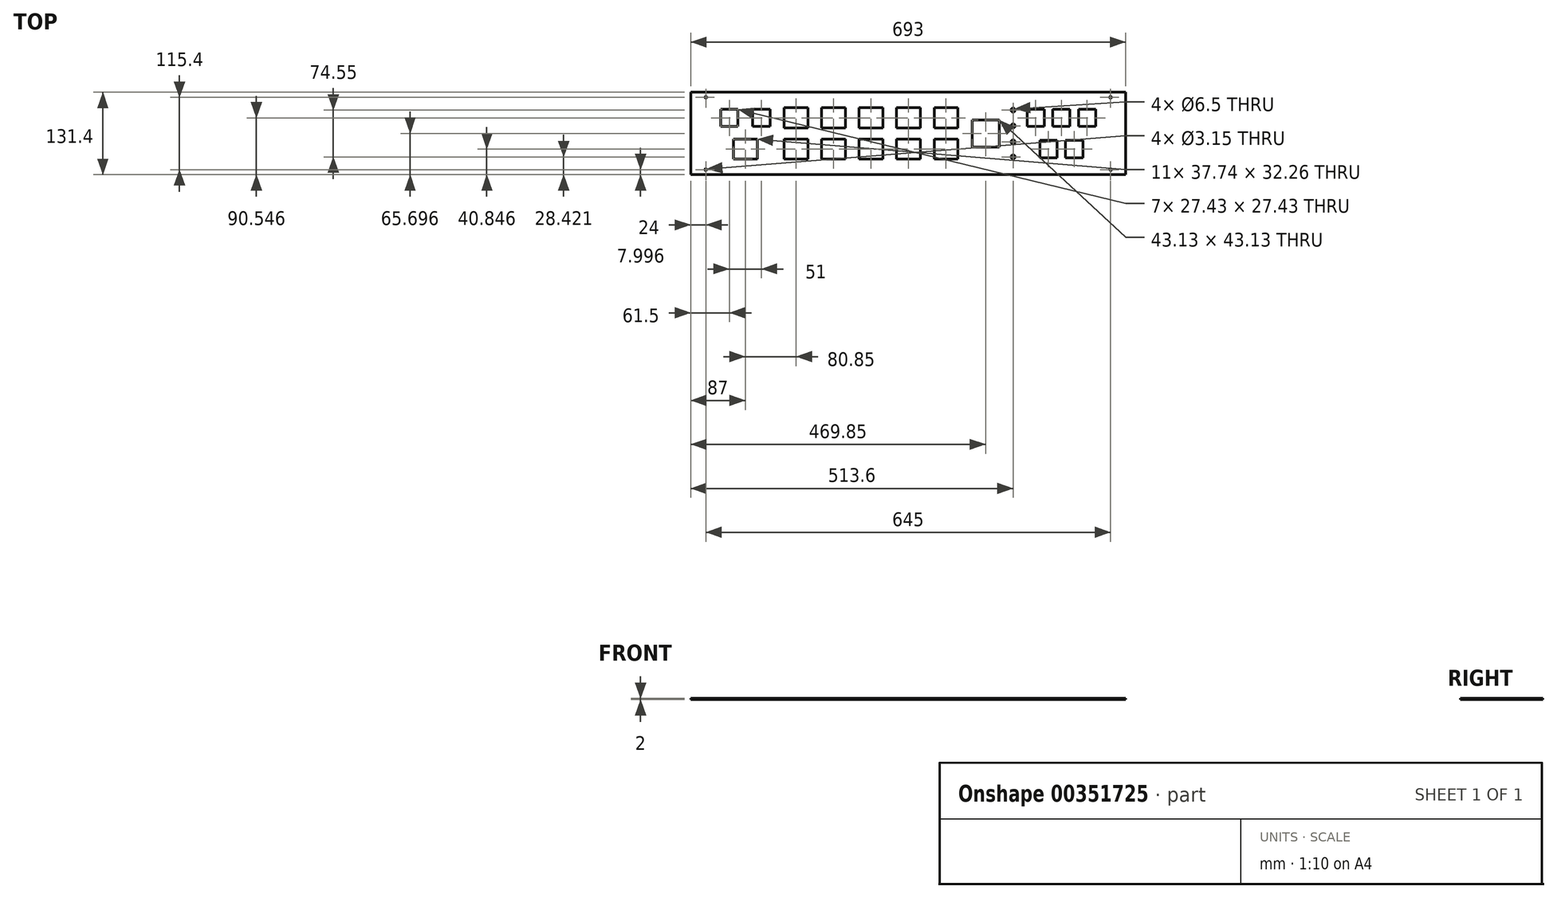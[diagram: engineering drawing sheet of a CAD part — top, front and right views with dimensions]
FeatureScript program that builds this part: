
annotation { "Feature Type Name" : "Feature", "Feature Type Description" : "" }
export const myFeature = defineFeature(function(context is Context, id is Id, definition is map)
    precondition{}
    {
        {
            var Q0;
            Q0=qCreatedBy(makeId("Top.planeOp"),FACE);
            var sketch = newSketch(context, id + "F0", { "sketchPlane" : qUnion([Q0])});
            skLineSegment(sketch, "E0.bottom", {"start": v(-326.44, 13.5) * mm, "end": v(366.56, 13.5) * mm});
            skLineSegment(sketch, "E0.top", {"start": v(-326.44, -117.9) * mm, "end": v(366.56, -117.9) * mm});
            skLineSegment(sketch, "E0.left", {"start": v(-326.44, 13.5) * mm, "end": v(-326.44, -117.9) * mm});
            skLineSegment(sketch, "E0.right", {"start": v(366.56, 13.5) * mm, "end": v(366.56, -117.9) * mm});
            skLineSegment(sketch, "E1", {"start": v(-310.44, 13.5) * mm, "end": v(-310.44, -117.9) * mm, "construction": true});
            skLineSegment(sketch, "E2", {"start": v(350.56, 13.5) * mm, "end": v(350.56, -117.9) * mm, "construction": true});
            skLineSegment(sketch, "E3", {"start": v(-326.44, -2.5) * mm, "end": v(366.56, -2.5) * mm, "construction": true});
            skLineSegment(sketch, "E4", {"start": v(-326.44, -101.9) * mm, "end": v(366.56, -101.9) * mm, "construction": true});
            skLineSegment(sketch, "E5", {"start": v(-326.44, -52.2) * mm, "end": v(366.56, -52.2) * mm, "construction": true});
            skLineSegment(sketch, "E6", {"start": v(-326.44, -27.34) * mm, "end": v(366.56, -27.34) * mm, "construction": true});
            skLineSegment(sketch, "E7", {"start": v(-326.44, -77.04) * mm, "end": v(366.56, -77.04) * mm, "construction": true});
            skLineSegment(sketch, "E8.bottom", {"start": v(-278.65, -13.63) * mm, "end": v(-251.22, -13.63) * mm});
            skLineSegment(sketch, "E8.top", {"start": v(-278.65, -41.06) * mm, "end": v(-251.22, -41.06) * mm});
            skLineSegment(sketch, "E8.left", {"start": v(-278.65, -13.63) * mm, "end": v(-278.65, -41.06) * mm});
            skLineSegment(sketch, "E8.right", {"start": v(-251.22, -13.63) * mm, "end": v(-251.22, -41.06) * mm});
            skLineSegment(sketch, "E9.bottom", {"start": v(-280.44, -11.84) * mm, "end": v(-249.44, -11.84) * mm, "construction": true});
            skLineSegment(sketch, "E9.top", {"start": v(-280.44, -42.84) * mm, "end": v(-249.44, -42.84) * mm, "construction": true});
            skLineSegment(sketch, "E9.left", {"start": v(-280.44, -11.84) * mm, "end": v(-280.44, -42.84) * mm, "construction": true});
            skLineSegment(sketch, "E9.right", {"start": v(-249.44, -11.84) * mm, "end": v(-249.44, -42.84) * mm, "construction": true});
            skLineSegment(sketch, "E10", {"start": v(-251.22, -13.63) * mm, "end": v(-278.65, -41.06) * mm, "construction": true});
            skPoint(sketch, "E11", {"position": v(-264.94, -27.34) * mm});
            skLineSegment(sketch, "E12", {"start": v(-280.44, -11.84) * mm, "end": v(-249.44, -42.84) * mm, "construction": true});
            skLineSegment(sketch, "E13.bottom", {"start": v(-227.65, -13.63) * mm, "end": v(-200.22, -13.63) * mm});
            skLineSegment(sketch, "E13.top", {"start": v(-227.65, -41.06) * mm, "end": v(-200.22, -41.06) * mm});
            skLineSegment(sketch, "E13.left", {"start": v(-227.65, -13.63) * mm, "end": v(-227.65, -41.06) * mm});
            skLineSegment(sketch, "E13.right", {"start": v(-200.22, -13.63) * mm, "end": v(-200.22, -41.06) * mm});
            skLineSegment(sketch, "E14.bottom", {"start": v(-229.44, -11.84) * mm, "end": v(-198.44, -11.84) * mm, "construction": true});
            skLineSegment(sketch, "E14.top", {"start": v(-229.44, -42.84) * mm, "end": v(-198.44, -42.84) * mm, "construction": true});
            skLineSegment(sketch, "E14.left", {"start": v(-229.44, -11.84) * mm, "end": v(-229.44, -42.84) * mm, "construction": true});
            skLineSegment(sketch, "E14.right", {"start": v(-198.44, -11.84) * mm, "end": v(-198.44, -42.84) * mm, "construction": true});
            skLineSegment(sketch, "E15", {"start": v(-200.22, -13.63) * mm, "end": v(-227.65, -41.06) * mm, "construction": true});
            skPoint(sketch, "E16", {"position": v(-213.94, -27.34) * mm});
            skLineSegment(sketch, "E17", {"start": v(-229.44, -11.84) * mm, "end": v(-198.44, -42.84) * mm, "construction": true});
            skLineSegment(sketch, "E18.bottom", {"start": v(-259.29, -59.7) * mm, "end": v(-219.59, -59.7) * mm, "construction": true});
            skLineSegment(sketch, "E18.top", {"start": v(-259.29, -94.4) * mm, "end": v(-219.59, -94.4) * mm, "construction": true});
            skLineSegment(sketch, "E18.left", {"start": v(-259.29, -59.7) * mm, "end": v(-259.29, -94.4) * mm, "construction": true});
            skLineSegment(sketch, "E18.right", {"start": v(-219.59, -59.7) * mm, "end": v(-219.59, -94.4) * mm, "construction": true});
            skLineSegment(sketch, "E19.bottom", {"start": v(-258.3, -60.91) * mm, "end": v(-220.57, -60.91) * mm});
            skLineSegment(sketch, "E19.top", {"start": v(-258.3, -93.17) * mm, "end": v(-220.57, -93.17) * mm});
            skLineSegment(sketch, "E19.left", {"start": v(-258.3, -60.91) * mm, "end": v(-258.3, -93.17) * mm});
            skLineSegment(sketch, "E19.right", {"start": v(-220.57, -60.91) * mm, "end": v(-220.57, -93.17) * mm});
            skLineSegment(sketch, "E20", {"start": v(-259.29, -59.7) * mm, "end": v(-219.59, -94.4) * mm, "construction": true});
            skLineSegment(sketch, "E21", {"start": v(-220.57, -60.91) * mm, "end": v(-258.3, -93.17) * mm, "construction": true});
            skPoint(sketch, "E22", {"position": v(-239.44, -77.04) * mm});
            skLineSegment(sketch, "E23", {"start": v(-249.44, -11.84) * mm, "end": v(-229.44, -11.84) * mm, "construction": true});
            skPoint(sketch, "E24", {"position": v(-239.44, -11.84) * mm});
            skLineSegment(sketch, "E25", {"start": v(-239.44, -11.84) * mm, "end": v(-239.44, -77.04) * mm, "construction": true});
            skLineSegment(sketch, "E26.bottom", {"start": v(-178.44, -59.7) * mm, "end": v(-138.74, -59.7) * mm, "construction": true});
            skLineSegment(sketch, "E26.top", {"start": v(-178.44, -94.4) * mm, "end": v(-138.74, -94.4) * mm, "construction": true});
            skLineSegment(sketch, "E26.left", {"start": v(-178.44, -59.7) * mm, "end": v(-178.44, -94.4) * mm, "construction": true});
            skLineSegment(sketch, "E26.right", {"start": v(-138.74, -59.7) * mm, "end": v(-138.74, -94.4) * mm, "construction": true});
            skLineSegment(sketch, "E27.bottom", {"start": v(-177.46, -60.91) * mm, "end": v(-139.72, -60.91) * mm});
            skLineSegment(sketch, "E27.top", {"start": v(-177.46, -93.17) * mm, "end": v(-139.72, -93.17) * mm});
            skLineSegment(sketch, "E27.left", {"start": v(-177.46, -60.91) * mm, "end": v(-177.46, -93.17) * mm});
            skLineSegment(sketch, "E27.right", {"start": v(-139.72, -60.91) * mm, "end": v(-139.72, -93.17) * mm});
            skLineSegment(sketch, "E28", {"start": v(-178.44, -59.7) * mm, "end": v(-138.74, -94.4) * mm, "construction": true});
            skLineSegment(sketch, "E29", {"start": v(-139.72, -60.91) * mm, "end": v(-177.46, -93.17) * mm, "construction": true});
            skPoint(sketch, "E30", {"position": v(-158.59, -77.04) * mm});
            skLineSegment(sketch, "E31.bottom", {"start": v(-118.74, -59.7) * mm, "end": v(-79.04, -59.7) * mm, "construction": true});
            skLineSegment(sketch, "E31.top", {"start": v(-118.74, -94.4) * mm, "end": v(-79.04, -94.4) * mm, "construction": true});
            skLineSegment(sketch, "E31.left", {"start": v(-118.74, -59.7) * mm, "end": v(-118.74, -94.4) * mm, "construction": true});
            skLineSegment(sketch, "E31.right", {"start": v(-79.04, -59.7) * mm, "end": v(-79.04, -94.4) * mm, "construction": true});
            skLineSegment(sketch, "E32.bottom", {"start": v(-117.76, -60.91) * mm, "end": v(-80.02, -60.91) * mm});
            skLineSegment(sketch, "E32.top", {"start": v(-117.76, -93.17) * mm, "end": v(-80.02, -93.17) * mm});
            skLineSegment(sketch, "E32.left", {"start": v(-117.76, -60.91) * mm, "end": v(-117.76, -93.17) * mm});
            skLineSegment(sketch, "E32.right", {"start": v(-80.02, -60.91) * mm, "end": v(-80.02, -93.17) * mm});
            skLineSegment(sketch, "E33", {"start": v(-118.74, -59.7) * mm, "end": v(-79.04, -94.4) * mm, "construction": true});
            skLineSegment(sketch, "E34", {"start": v(-80.02, -60.91) * mm, "end": v(-117.76, -93.17) * mm, "construction": true});
            skPoint(sketch, "E35", {"position": v(-98.89, -77.04) * mm});
            skLineSegment(sketch, "E36.bottom", {"start": v(-59.04, -59.7) * mm, "end": v(-19.34, -59.7) * mm, "construction": true});
            skLineSegment(sketch, "E36.top", {"start": v(-59.04, -94.4) * mm, "end": v(-19.34, -94.4) * mm, "construction": true});
            skLineSegment(sketch, "E36.left", {"start": v(-59.04, -59.7) * mm, "end": v(-59.04, -94.4) * mm, "construction": true});
            skLineSegment(sketch, "E36.right", {"start": v(-19.34, -59.7) * mm, "end": v(-19.34, -94.4) * mm, "construction": true});
            skLineSegment(sketch, "E37.bottom", {"start": v(-58.06, -60.91) * mm, "end": v(-20.32, -60.91) * mm});
            skLineSegment(sketch, "E37.top", {"start": v(-58.06, -93.17) * mm, "end": v(-20.32, -93.17) * mm});
            skLineSegment(sketch, "E37.left", {"start": v(-58.06, -60.91) * mm, "end": v(-58.06, -93.17) * mm});
            skLineSegment(sketch, "E37.right", {"start": v(-20.32, -60.91) * mm, "end": v(-20.32, -93.17) * mm});
            skLineSegment(sketch, "E38", {"start": v(-59.04, -59.7) * mm, "end": v(-19.34, -94.4) * mm, "construction": true});
            skLineSegment(sketch, "E39", {"start": v(-20.32, -60.91) * mm, "end": v(-58.06, -93.17) * mm, "construction": true});
            skPoint(sketch, "E40", {"position": v(-39.19, -77.04) * mm});
            skLineSegment(sketch, "E41.bottom", {"start": v(0.66, -59.7) * mm, "end": v(40.36, -59.7) * mm, "construction": true});
            skLineSegment(sketch, "E41.top", {"start": v(0.66, -94.4) * mm, "end": v(40.36, -94.4) * mm, "construction": true});
            skLineSegment(sketch, "E41.left", {"start": v(0.66, -59.7) * mm, "end": v(0.66, -94.4) * mm, "construction": true});
            skLineSegment(sketch, "E41.right", {"start": v(40.36, -59.7) * mm, "end": v(40.36, -94.4) * mm, "construction": true});
            skLineSegment(sketch, "E42.bottom", {"start": v(1.64, -60.91) * mm, "end": v(39.38, -60.91) * mm});
            skLineSegment(sketch, "E42.top", {"start": v(1.64, -93.17) * mm, "end": v(39.38, -93.17) * mm});
            skLineSegment(sketch, "E42.left", {"start": v(1.64, -60.91) * mm, "end": v(1.64, -93.17) * mm});
            skLineSegment(sketch, "E42.right", {"start": v(39.38, -60.91) * mm, "end": v(39.38, -93.17) * mm});
            skLineSegment(sketch, "E43", {"start": v(0.66, -59.7) * mm, "end": v(40.36, -94.4) * mm, "construction": true});
            skLineSegment(sketch, "E44", {"start": v(39.38, -60.91) * mm, "end": v(1.64, -93.17) * mm, "construction": true});
            skPoint(sketch, "E45", {"position": v(20.51, -77.04) * mm});
            skLineSegment(sketch, "E46.bottom", {"start": v(60.36, -59.7) * mm, "end": v(100.06, -59.7) * mm, "construction": true});
            skLineSegment(sketch, "E46.top", {"start": v(60.36, -94.4) * mm, "end": v(100.06, -94.4) * mm, "construction": true});
            skLineSegment(sketch, "E46.left", {"start": v(60.36, -59.7) * mm, "end": v(60.36, -94.4) * mm, "construction": true});
            skLineSegment(sketch, "E46.right", {"start": v(100.06, -59.7) * mm, "end": v(100.06, -94.4) * mm, "construction": true});
            skLineSegment(sketch, "E47.bottom", {"start": v(61.34, -60.91) * mm, "end": v(99.08, -60.91) * mm});
            skLineSegment(sketch, "E47.top", {"start": v(61.34, -93.17) * mm, "end": v(99.08, -93.17) * mm});
            skLineSegment(sketch, "E47.left", {"start": v(61.34, -60.91) * mm, "end": v(61.34, -93.17) * mm});
            skLineSegment(sketch, "E47.right", {"start": v(99.08, -60.91) * mm, "end": v(99.08, -93.17) * mm});
            skLineSegment(sketch, "E48", {"start": v(60.36, -59.7) * mm, "end": v(100.06, -94.4) * mm, "construction": true});
            skLineSegment(sketch, "E49", {"start": v(99.08, -60.91) * mm, "end": v(61.34, -93.17) * mm, "construction": true});
            skPoint(sketch, "E50", {"position": v(80.21, -77.04) * mm});
            skLineSegment(sketch, "E51.bottom", {"start": v(-178.44, -10) * mm, "end": v(-138.74, -10) * mm, "construction": true});
            skLineSegment(sketch, "E51.top", {"start": v(-178.44, -44.7) * mm, "end": v(-138.74, -44.7) * mm, "construction": true});
            skLineSegment(sketch, "E51.left", {"start": v(-178.44, -10) * mm, "end": v(-178.44, -44.7) * mm, "construction": true});
            skLineSegment(sketch, "E51.right", {"start": v(-138.74, -10) * mm, "end": v(-138.74, -44.7) * mm, "construction": true});
            skLineSegment(sketch, "E52.bottom", {"start": v(-177.46, -11.21) * mm, "end": v(-139.72, -11.21) * mm});
            skLineSegment(sketch, "E52.top", {"start": v(-177.46, -43.47) * mm, "end": v(-139.72, -43.47) * mm});
            skLineSegment(sketch, "E52.left", {"start": v(-177.46, -11.21) * mm, "end": v(-177.46, -43.47) * mm});
            skLineSegment(sketch, "E52.right", {"start": v(-139.72, -11.21) * mm, "end": v(-139.72, -43.47) * mm});
            skLineSegment(sketch, "E53", {"start": v(-178.44, -10) * mm, "end": v(-138.74, -44.7) * mm, "construction": true});
            skLineSegment(sketch, "E54", {"start": v(-139.72, -11.21) * mm, "end": v(-177.46, -43.47) * mm, "construction": true});
            skPoint(sketch, "E55", {"position": v(-158.59, -27.34) * mm});
            skLineSegment(sketch, "E56.bottom", {"start": v(-118.74, -10) * mm, "end": v(-79.04, -10) * mm, "construction": true});
            skLineSegment(sketch, "E56.top", {"start": v(-118.74, -44.7) * mm, "end": v(-79.04, -44.7) * mm, "construction": true});
            skLineSegment(sketch, "E56.left", {"start": v(-118.74, -10) * mm, "end": v(-118.74, -44.7) * mm, "construction": true});
            skLineSegment(sketch, "E56.right", {"start": v(-79.04, -10) * mm, "end": v(-79.04, -44.7) * mm, "construction": true});
            skLineSegment(sketch, "E57.bottom", {"start": v(-117.76, -11.21) * mm, "end": v(-80.02, -11.21) * mm});
            skLineSegment(sketch, "E57.top", {"start": v(-117.76, -43.47) * mm, "end": v(-80.02, -43.47) * mm});
            skLineSegment(sketch, "E57.left", {"start": v(-117.76, -11.21) * mm, "end": v(-117.76, -43.47) * mm});
            skLineSegment(sketch, "E57.right", {"start": v(-80.02, -11.21) * mm, "end": v(-80.02, -43.47) * mm});
            skLineSegment(sketch, "E58", {"start": v(-118.74, -10) * mm, "end": v(-79.04, -44.7) * mm, "construction": true});
            skLineSegment(sketch, "E59", {"start": v(-80.02, -11.21) * mm, "end": v(-117.76, -43.47) * mm, "construction": true});
            skPoint(sketch, "E60", {"position": v(-98.89, -27.34) * mm});
            skLineSegment(sketch, "E61.bottom", {"start": v(-59.04, -10) * mm, "end": v(-19.34, -10) * mm, "construction": true});
            skLineSegment(sketch, "E61.top", {"start": v(-59.04, -44.7) * mm, "end": v(-19.34, -44.7) * mm, "construction": true});
            skLineSegment(sketch, "E61.left", {"start": v(-59.04, -10) * mm, "end": v(-59.04, -44.7) * mm, "construction": true});
            skLineSegment(sketch, "E61.right", {"start": v(-19.34, -10) * mm, "end": v(-19.34, -44.7) * mm, "construction": true});
            skLineSegment(sketch, "E62.bottom", {"start": v(-58.06, -11.21) * mm, "end": v(-20.32, -11.21) * mm});
            skLineSegment(sketch, "E62.top", {"start": v(-58.06, -43.47) * mm, "end": v(-20.32, -43.47) * mm});
            skLineSegment(sketch, "E62.left", {"start": v(-58.06, -11.21) * mm, "end": v(-58.06, -43.47) * mm});
            skLineSegment(sketch, "E62.right", {"start": v(-20.32, -11.21) * mm, "end": v(-20.32, -43.47) * mm});
            skLineSegment(sketch, "E63", {"start": v(-59.04, -10) * mm, "end": v(-19.34, -44.7) * mm, "construction": true});
            skLineSegment(sketch, "E64", {"start": v(-20.32, -11.21) * mm, "end": v(-58.06, -43.47) * mm, "construction": true});
            skPoint(sketch, "E65", {"position": v(-39.19, -27.34) * mm});
            skLineSegment(sketch, "E66.bottom", {"start": v(0.66, -10) * mm, "end": v(40.36, -10) * mm, "construction": true});
            skLineSegment(sketch, "E66.top", {"start": v(0.66, -44.7) * mm, "end": v(40.36, -44.7) * mm, "construction": true});
            skLineSegment(sketch, "E66.left", {"start": v(0.66, -10) * mm, "end": v(0.66, -44.7) * mm, "construction": true});
            skLineSegment(sketch, "E66.right", {"start": v(40.36, -10) * mm, "end": v(40.36, -44.7) * mm, "construction": true});
            skLineSegment(sketch, "E67.bottom", {"start": v(1.64, -11.21) * mm, "end": v(39.38, -11.21) * mm});
            skLineSegment(sketch, "E67.top", {"start": v(1.64, -43.47) * mm, "end": v(39.38, -43.47) * mm});
            skLineSegment(sketch, "E67.left", {"start": v(1.64, -11.21) * mm, "end": v(1.64, -43.47) * mm});
            skLineSegment(sketch, "E67.right", {"start": v(39.38, -11.21) * mm, "end": v(39.38, -43.47) * mm});
            skLineSegment(sketch, "E68", {"start": v(0.66, -10) * mm, "end": v(40.36, -44.7) * mm, "construction": true});
            skLineSegment(sketch, "E69", {"start": v(39.38, -11.21) * mm, "end": v(1.64, -43.47) * mm, "construction": true});
            skPoint(sketch, "E70", {"position": v(20.51, -27.34) * mm});
            skLineSegment(sketch, "E71.bottom", {"start": v(60.36, -10) * mm, "end": v(100.06, -10) * mm, "construction": true});
            skLineSegment(sketch, "E71.top", {"start": v(60.36, -44.7) * mm, "end": v(100.06, -44.7) * mm, "construction": true});
            skLineSegment(sketch, "E71.left", {"start": v(60.36, -10) * mm, "end": v(60.36, -44.7) * mm, "construction": true});
            skLineSegment(sketch, "E71.right", {"start": v(100.06, -10) * mm, "end": v(100.06, -44.7) * mm, "construction": true});
            skLineSegment(sketch, "E72.bottom", {"start": v(61.34, -11.21) * mm, "end": v(99.08, -11.21) * mm});
            skLineSegment(sketch, "E72.top", {"start": v(61.34, -43.47) * mm, "end": v(99.08, -43.47) * mm});
            skLineSegment(sketch, "E72.left", {"start": v(61.34, -11.21) * mm, "end": v(61.34, -43.47) * mm});
            skLineSegment(sketch, "E72.right", {"start": v(99.08, -11.21) * mm, "end": v(99.08, -43.47) * mm});
            skLineSegment(sketch, "E73", {"start": v(60.36, -10) * mm, "end": v(100.06, -44.7) * mm, "construction": true});
            skLineSegment(sketch, "E74", {"start": v(99.08, -11.21) * mm, "end": v(61.34, -43.47) * mm, "construction": true});
            skPoint(sketch, "E75", {"position": v(80.21, -27.34) * mm});
            skLineSegment(sketch, "E76.bottom", {"start": v(120.06, -28.84) * mm, "end": v(166.76, -28.84) * mm, "construction": true});
            skLineSegment(sketch, "E76.top", {"start": v(120.06, -75.54) * mm, "end": v(166.76, -75.54) * mm, "construction": true});
            skLineSegment(sketch, "E76.left", {"start": v(120.06, -28.84) * mm, "end": v(120.06, -75.54) * mm, "construction": true});
            skLineSegment(sketch, "E76.right", {"start": v(166.76, -28.84) * mm, "end": v(166.76, -75.54) * mm, "construction": true});
            skLineSegment(sketch, "E77.bottom", {"start": v(121.85, -30.63) * mm, "end": v(164.98, -30.63) * mm});
            skLineSegment(sketch, "E77.top", {"start": v(121.85, -73.76) * mm, "end": v(164.98, -73.76) * mm});
            skLineSegment(sketch, "E77.left", {"start": v(121.85, -30.63) * mm, "end": v(121.85, -73.76) * mm});
            skLineSegment(sketch, "E77.right", {"start": v(164.98, -30.63) * mm, "end": v(164.98, -73.76) * mm});
            skLineSegment(sketch, "E78", {"start": v(120.06, -28.84) * mm, "end": v(166.76, -75.54) * mm, "construction": true});
            skLineSegment(sketch, "E79", {"start": v(164.98, -30.63) * mm, "end": v(121.85, -73.76) * mm, "construction": true});
            skPoint(sketch, "E80", {"position": v(143.41, -52.2) * mm});
            skLineSegment(sketch, "E81.bottom", {"start": v(291.35, -13.63) * mm, "end": v(318.78, -13.63) * mm});
            skLineSegment(sketch, "E81.top", {"start": v(291.35, -41.06) * mm, "end": v(318.78, -41.06) * mm});
            skLineSegment(sketch, "E81.left", {"start": v(291.35, -13.63) * mm, "end": v(291.35, -41.06) * mm});
            skLineSegment(sketch, "E81.right", {"start": v(318.78, -13.63) * mm, "end": v(318.78, -41.06) * mm});
            skLineSegment(sketch, "E82.bottom", {"start": v(289.56, -11.84) * mm, "end": v(320.56, -11.84) * mm, "construction": true});
            skLineSegment(sketch, "E82.top", {"start": v(289.56, -42.84) * mm, "end": v(320.56, -42.84) * mm, "construction": true});
            skLineSegment(sketch, "E82.left", {"start": v(289.56, -11.84) * mm, "end": v(289.56, -42.84) * mm, "construction": true});
            skLineSegment(sketch, "E82.right", {"start": v(320.56, -11.84) * mm, "end": v(320.56, -42.84) * mm, "construction": true});
            skLineSegment(sketch, "E83", {"start": v(318.78, -13.63) * mm, "end": v(291.35, -41.06) * mm, "construction": true});
            skPoint(sketch, "E84", {"position": v(305.06, -27.34) * mm});
            skLineSegment(sketch, "E85", {"start": v(289.56, -11.84) * mm, "end": v(320.56, -42.84) * mm, "construction": true});
            skLineSegment(sketch, "E86.bottom", {"start": v(250.35, -13.63) * mm, "end": v(277.78, -13.63) * mm});
            skLineSegment(sketch, "E86.top", {"start": v(250.35, -41.06) * mm, "end": v(277.78, -41.06) * mm});
            skLineSegment(sketch, "E86.left", {"start": v(250.35, -13.63) * mm, "end": v(250.35, -41.06) * mm});
            skLineSegment(sketch, "E86.right", {"start": v(277.78, -13.63) * mm, "end": v(277.78, -41.06) * mm});
            skLineSegment(sketch, "E87.bottom", {"start": v(248.56, -11.84) * mm, "end": v(279.56, -11.84) * mm, "construction": true});
            skLineSegment(sketch, "E87.top", {"start": v(248.56, -42.84) * mm, "end": v(279.56, -42.84) * mm, "construction": true});
            skLineSegment(sketch, "E87.left", {"start": v(248.56, -11.84) * mm, "end": v(248.56, -42.84) * mm, "construction": true});
            skLineSegment(sketch, "E87.right", {"start": v(279.56, -11.84) * mm, "end": v(279.56, -42.84) * mm, "construction": true});
            skLineSegment(sketch, "E88", {"start": v(277.78, -13.63) * mm, "end": v(250.35, -41.06) * mm, "construction": true});
            skPoint(sketch, "E89", {"position": v(264.06, -27.34) * mm});
            skLineSegment(sketch, "E90", {"start": v(248.56, -11.84) * mm, "end": v(279.56, -42.84) * mm, "construction": true});
            skLineSegment(sketch, "E91.bottom", {"start": v(209.35, -13.63) * mm, "end": v(236.78, -13.63) * mm});
            skLineSegment(sketch, "E91.top", {"start": v(209.35, -41.06) * mm, "end": v(236.78, -41.06) * mm});
            skLineSegment(sketch, "E91.left", {"start": v(209.35, -13.63) * mm, "end": v(209.35, -41.06) * mm});
            skLineSegment(sketch, "E91.right", {"start": v(236.78, -13.63) * mm, "end": v(236.78, -41.06) * mm});
            skLineSegment(sketch, "E92.bottom", {"start": v(207.56, -11.84) * mm, "end": v(238.56, -11.84) * mm, "construction": true});
            skLineSegment(sketch, "E92.top", {"start": v(207.56, -42.84) * mm, "end": v(238.56, -42.84) * mm, "construction": true});
            skLineSegment(sketch, "E92.left", {"start": v(207.56, -11.84) * mm, "end": v(207.56, -42.84) * mm, "construction": true});
            skLineSegment(sketch, "E92.right", {"start": v(238.56, -11.84) * mm, "end": v(238.56, -42.84) * mm, "construction": true});
            skLineSegment(sketch, "E93", {"start": v(236.78, -13.63) * mm, "end": v(209.35, -41.06) * mm, "construction": true});
            skPoint(sketch, "E94", {"position": v(223.06, -27.34) * mm});
            skLineSegment(sketch, "E95", {"start": v(207.56, -11.84) * mm, "end": v(238.56, -42.84) * mm, "construction": true});
            skLineSegment(sketch, "E96", {"start": v(238.56, -11.84) * mm, "end": v(248.56, -11.84) * mm, "construction": true});
            skLineSegment(sketch, "E97", {"start": v(279.56, -11.84) * mm, "end": v(289.56, -11.84) * mm, "construction": true});
            skPoint(sketch, "E98", {"position": v(284.56, -11.84) * mm});
            skPoint(sketch, "E99", {"position": v(243.56, -11.84) * mm});
            skLineSegment(sketch, "E100.bottom", {"start": v(229.85, -63.33) * mm, "end": v(257.28, -63.33) * mm});
            skLineSegment(sketch, "E100.top", {"start": v(229.85, -90.76) * mm, "end": v(257.28, -90.76) * mm});
            skLineSegment(sketch, "E100.left", {"start": v(229.85, -63.33) * mm, "end": v(229.85, -90.76) * mm});
            skLineSegment(sketch, "E100.right", {"start": v(257.28, -63.33) * mm, "end": v(257.28, -90.76) * mm});
            skLineSegment(sketch, "E101.bottom", {"start": v(228.06, -61.54) * mm, "end": v(259.06, -61.54) * mm, "construction": true});
            skLineSegment(sketch, "E101.top", {"start": v(228.06, -92.54) * mm, "end": v(259.06, -92.54) * mm, "construction": true});
            skLineSegment(sketch, "E101.left", {"start": v(228.06, -61.54) * mm, "end": v(228.06, -92.54) * mm, "construction": true});
            skLineSegment(sketch, "E101.right", {"start": v(259.06, -61.54) * mm, "end": v(259.06, -92.54) * mm, "construction": true});
            skLineSegment(sketch, "E102", {"start": v(257.28, -63.33) * mm, "end": v(229.85, -90.76) * mm, "construction": true});
            skPoint(sketch, "E103", {"position": v(243.56, -77.04) * mm});
            skLineSegment(sketch, "E104", {"start": v(228.06, -61.54) * mm, "end": v(259.06, -92.54) * mm, "construction": true});
            skLineSegment(sketch, "E105", {"start": v(243.56, -11.84) * mm, "end": v(243.56, -77.04) * mm, "construction": true});
            skLineSegment(sketch, "E106.bottom", {"start": v(270.85, -63.33) * mm, "end": v(298.28, -63.33) * mm});
            skLineSegment(sketch, "E106.top", {"start": v(270.85, -90.76) * mm, "end": v(298.28, -90.76) * mm});
            skLineSegment(sketch, "E106.left", {"start": v(270.85, -63.33) * mm, "end": v(270.85, -90.76) * mm});
            skLineSegment(sketch, "E106.right", {"start": v(298.28, -63.33) * mm, "end": v(298.28, -90.76) * mm});
            skLineSegment(sketch, "E107.bottom", {"start": v(269.06, -61.54) * mm, "end": v(300.06, -61.54) * mm, "construction": true});
            skLineSegment(sketch, "E107.top", {"start": v(269.06, -92.54) * mm, "end": v(300.06, -92.54) * mm, "construction": true});
            skLineSegment(sketch, "E107.left", {"start": v(269.06, -61.54) * mm, "end": v(269.06, -92.54) * mm, "construction": true});
            skLineSegment(sketch, "E107.right", {"start": v(300.06, -61.54) * mm, "end": v(300.06, -92.54) * mm, "construction": true});
            skLineSegment(sketch, "E108", {"start": v(298.28, -63.33) * mm, "end": v(270.85, -90.76) * mm, "construction": true});
            skPoint(sketch, "E109", {"position": v(284.56, -77.04) * mm});
            skLineSegment(sketch, "E110", {"start": v(269.06, -61.54) * mm, "end": v(300.06, -92.54) * mm, "construction": true});
            skLineSegment(sketch, "E111", {"start": v(284.56, -11.84) * mm, "end": v(284.56, -77.04) * mm, "construction": true});
            skPoint(sketch, "E112", {"position": v(187.16, -14.92) * mm});
            skPoint(sketch, "E113", {"position": v(187.16, -40.08) * mm});
            skPoint(sketch, "E114", {"position": v(187.16, -65.72) * mm});
            skPoint(sketch, "E115", {"position": v(187.16, -89.47) * mm});
            skCircle(sketch, "E116", {"center": v(187.16, -14.92) * mm, "radius": 4 * mm, "construction": true});
            skCircle(sketch, "E117", {"center": v(187.16, -14.92) * mm, "radius": 3.25 * mm});
            skCircle(sketch, "E118", {"center": v(187.16, -40.08) * mm, "radius": 4 * mm, "construction": true});
            skCircle(sketch, "E119", {"center": v(187.16, -40.08) * mm, "radius": 3.25 * mm});
            skCircle(sketch, "E120", {"center": v(187.16, -65.72) * mm, "radius": 4 * mm, "construction": true});
            skCircle(sketch, "E121", {"center": v(187.16, -65.72) * mm, "radius": 3.25 * mm});
            skCircle(sketch, "E122", {"center": v(187.16, -89.47) * mm, "radius": 4 * mm, "construction": true});
            skCircle(sketch, "E123", {"center": v(187.16, -89.47) * mm, "radius": 3.25 * mm});
            skCircle(sketch, "E124", {"center": v(-302.44, 5.5) * mm, "radius": 1.57 * mm});
            skCircle(sketch, "E125", {"center": v(342.56, 5.5) * mm, "radius": 1.57 * mm});
            skCircle(sketch, "E126", {"center": v(342.56, -109.9) * mm, "radius": 1.57 * mm});
            skCircle(sketch, "E127", {"center": v(-302.44, -109.9) * mm, "radius": 1.57 * mm});
            skLineSegment(sketch, "E128", {"start": v(-302.44, 5.5) * mm, "end": v(342.56, 5.5) * mm, "construction": true});
            skLineSegment(sketch, "E129", {"start": v(342.56, 5.5) * mm, "end": v(342.56, -109.9) * mm, "construction": true});
            skLineSegment(sketch, "E130", {"start": v(342.56, -109.9) * mm, "end": v(-302.44, -109.9) * mm, "construction": true});
            skLineSegment(sketch, "E131", {"start": v(-302.44, -109.9) * mm, "end": v(-302.44, 5.5) * mm, "construction": true});
            skLineSegment(sketch, "E132", {"start": v(207.56, -11.84) * mm, "end": v(166.76, -11.84) * mm, "construction": true});
            skLineSegment(sketch, "E133", {"start": v(166.76, -11.84) * mm, "end": v(166.76, -28.84) * mm, "construction": true});
            skPoint(sketch, "E134", {"position": v(187.16, -11.84) * mm});
            skLineSegment(sketch, "E135", {"start": v(187.16, -11.84) * mm, "end": v(187.16, -14.92) * mm});
            skSolve(sketch);
        }
        {
            var Q0;
            Q0 = qSketchRegion(id + "F0", true);
            extrude(context, id + "F1", {"entities" : qUnion([Q0]), "depth" : 2 * mm});
        }
    });
